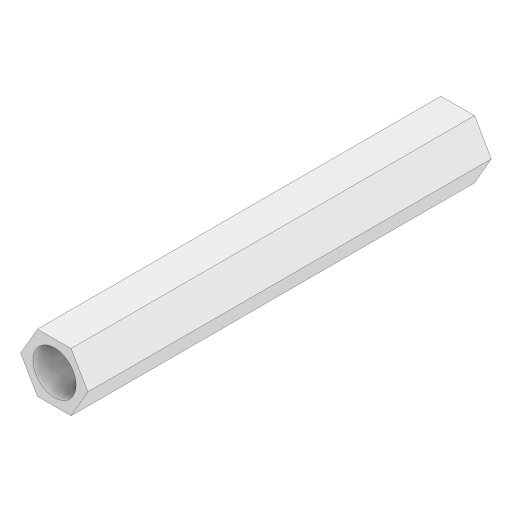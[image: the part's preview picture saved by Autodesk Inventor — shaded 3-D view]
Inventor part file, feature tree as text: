
AUTODESK INVENTOR PART (.ipt)
format: ipt  version: 2023.2 (Build 272271000, 271)  size: 99,840 bytes
history: native  units: mm
features: other x1, extrude x1, sketch x1
ambient origin geometry x8: Origin, YZ Plane, XZ Plane, XY Plane, X Axis, Y Axis, Z Axis, Center Point
bodies: Body1 (feature_tree)
feature tree (3):
  other  "솔리드1"
  extrude  "돌출1"  Depth=3.2mm
  sketch  "스케치1"
